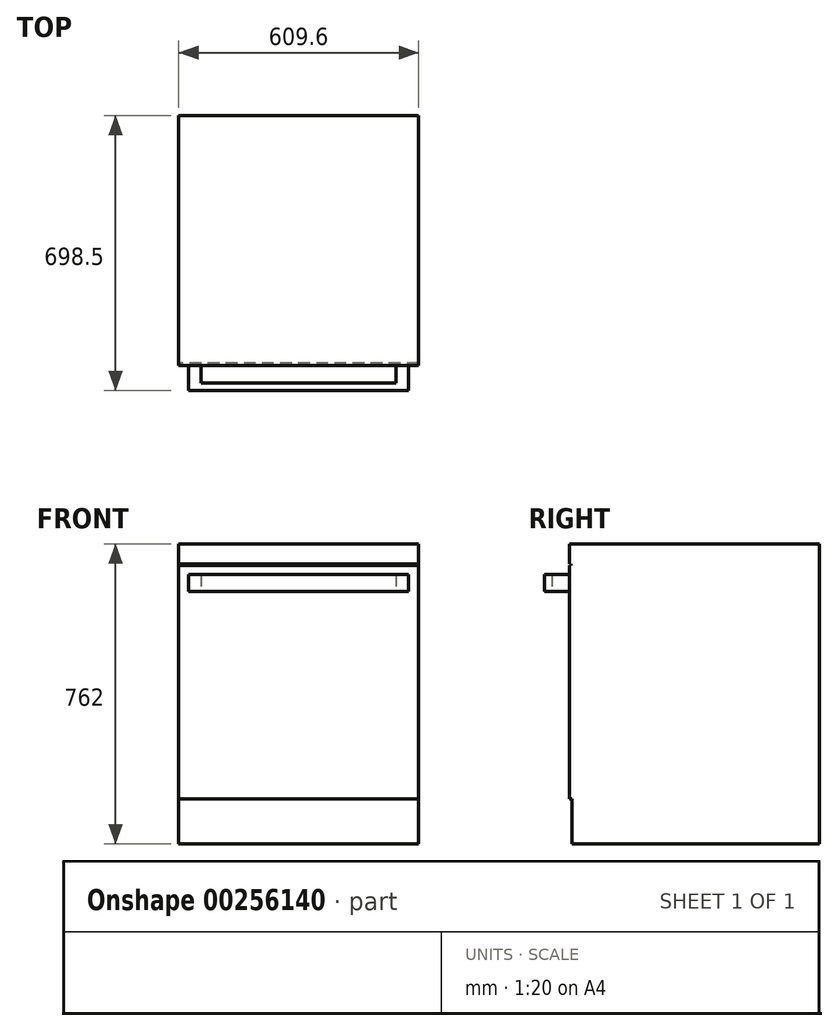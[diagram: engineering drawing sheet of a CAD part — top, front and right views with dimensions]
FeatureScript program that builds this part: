
annotation { "Feature Type Name" : "Feature", "Feature Type Description" : "" }
export const myFeature = defineFeature(function(context is Context, id is Id, definition is map)
    precondition{}
    {
        {
            var Q0;
            Q0=qCreatedBy(makeId("Right.planeOp"),FACE);
            var sketch = newSketch(context, id + "F0", { "sketchPlane" : qUnion([Q0])});
            skLineSegment(sketch, "E0", {"start": v(0, 0) * mm, "end": v(0, 762) * mm});
            skLineSegment(sketch, "E1", {"start": v(0, 0) * mm, "end": v(-628.65, 0) * mm});
            skLineSegment(sketch, "E2", {"start": v(-628.65, 0) * mm, "end": v(-628.65, 113.82) * mm});
            skLineSegment(sketch, "E3", {"start": v(-628.65, 113.82) * mm, "end": v(-635, 113.82) * mm});
            skLineSegment(sketch, "E4", {"start": v(-635, 113.82) * mm, "end": v(-635, 708.03) * mm});
            skLineSegment(sketch, "E5", {"start": v(-635, 708.03) * mm, "end": v(-631.82, 708.03) * mm});
            skLineSegment(sketch, "E6", {"start": v(-631.82, 708.03) * mm, "end": v(-631.82, 711.2) * mm});
            skLineSegment(sketch, "E7", {"start": v(-631.82, 711.2) * mm, "end": v(-635, 711.2) * mm});
            skLineSegment(sketch, "E8", {"start": v(-635, 711.2) * mm, "end": v(-635, 762) * mm});
            skLineSegment(sketch, "E9", {"start": v(-635, 762) * mm, "end": v(0, 762) * mm});
            skSolve(sketch);
        }
        {
            var Q0;
            Q0=makeQuery(id+"F0.imprint","IMPRINT",FACE,{"disambiguationData":[TD([[makeQuery(id+"F0.imprint","IMPRINT",EDGE,{"derivedFrom":sQuery(id+"F0.wireOp",EDGE,"E0")}),1.0]])]});
            extrude(context, id + "F1", {"entities" : qUnion([Q0]), "endBound" : BoundingType.SYMMETRIC, "depth" : 609.6 * mm});
        }
        {
            var Q0;
            Q0=qCreatedBy(makeId("Top.planeOp"),FACE);
            cPlane(context, id + "F2", {"entities" : qUnion([Q0]), "cplaneType" : CPlaneType.OFFSET, "offset" : 662.94 * mm, "width" : 152.4 * mm, "height" : 152.4 * mm});
        }
        {
            var Q0;
            Q0=qCreatedBy(id+"F2.planeOp",FACE);
            var sketch = newSketch(context, id + "F3", { "sketchPlane" : qUnion([Q0])});
            skLineSegment(sketch, "E10.bottom", {"start": v(279.4, -698.5) * mm, "end": v(-279.4, -698.5) * mm});
            skPoint(sketch, "E10.middle", {"position": v(0, -688.98) * mm});
            skLineSegment(sketch, "E11.top", {"start": v(-279.4, -609.34) * mm, "end": v(-247.65, -609.34) * mm});
            skLineSegment(sketch, "E11.left", {"start": v(-279.4, -698.5) * mm, "end": v(-279.4, -609.34) * mm});
            skLineSegment(sketch, "E11.right", {"start": v(-247.65, -679.45) * mm, "end": v(-247.65, -609.34) * mm});
            skLineSegment(sketch, "E12.MirrorCS", {"start": v(279.4, -698.5) * mm, "end": v(279.4, -609.34) * mm});
            skLineSegment(sketch, "E13.MirrorCS", {"start": v(247.65, -679.45) * mm, "end": v(247.65, -609.34) * mm});
            skLineSegment(sketch, "E14.MirrorCS", {"start": v(279.4, -609.34) * mm, "end": v(247.65, -609.34) * mm});
            skLineSegment(sketch, "E15", {"start": v(-247.65, -679.45) * mm, "end": v(247.65, -679.45) * mm});
            skSolve(sketch);
        }
        {
            var Q0;
            Q0=qSketchRegion(id+"F3",true);
            extrude(context, id + "F4", {"entities" : qUnion([Q0]), "operationType" : NewBodyOperationType.ADD, "endBound" : BoundingType.SYMMETRIC, "depth" : 43.18 * mm});
        }
    });
